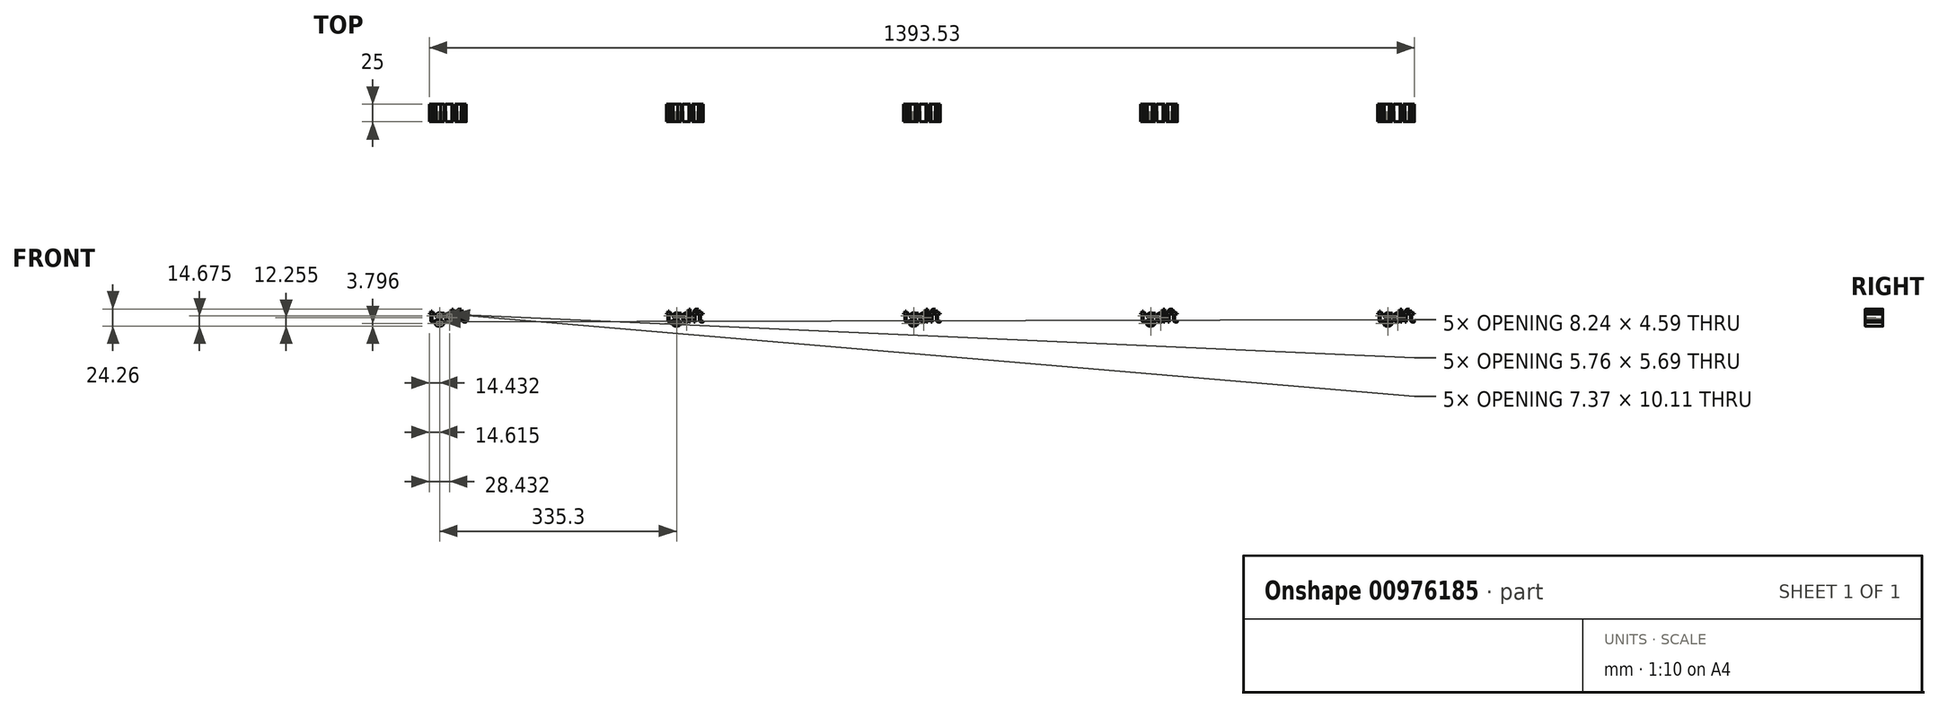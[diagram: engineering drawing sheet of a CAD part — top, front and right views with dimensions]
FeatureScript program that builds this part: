
annotation { "Feature Type Name" : "Feature", "Feature Type Description" : "" }
export const myFeature = defineFeature(function(context is Context, id is Id, definition is map)
    precondition{}
    {
        {
            var Q0;
            Q0=qCreatedBy(makeId("Front.planeOp"),FACE);
            var sketch = newSketch(context, id + "F0", { "sketchPlane" : qUnion([Q0])});
            skText(sketch, "E0", { "text": "                                             tgdft                                             tgdft                                             tgdft                                             tgdft                                             tgdft", "fontName": "OpenSans-Regular.ttf"});
            const initialGuessF0  = {"E0": [0, 0, 1, 0, 0.01737]};
            skSetInitialGuess(sketch, initialGuessF0);
            skSolve(sketch);
        }
        {
            var Q0;
            Q0 = qSketchRegion(id + "F0", true);
            extrude(context, id + "F1", {"entities" : qUnion([Q0]), "depth" : 25 * mm, "offsetDistance" : 25 * mm});
        }
    });
